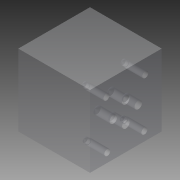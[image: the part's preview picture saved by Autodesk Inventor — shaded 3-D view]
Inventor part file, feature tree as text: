
AUTODESK INVENTOR PART (.ipt)
format: ipt  version: 2014 (Build 180170000, 170)  size: 209,920 bytes
history: native  units: mm
features: other x48, extrude x15, sketch x15
ambient origin geometry x8: Origin, YZ Plane, XZ Plane, XY Plane, X Axis, Y Axis, Z Axis, Center Point
bodies: 实体1 (feature_tree)
feature tree (78):
  extrude  "拉伸1"  Depth=51.0mm
  other  "UCS1"
  other  "UCS2"
  other  "UCS3"
  other  "UCS4"
  other  "UCS5"
  other  "UCS6"
  extrude  "拉伸2"  Depth=30.0mm
  extrude  "拉伸3"  Depth=4.25mm
  extrude  "拉伸4"  Depth=21.5mm
  extrude  "拉伸5"  Depth=0.75mm
  extrude  "拉伸6"  TaperAngle=0.0deg  [1 undecoded]
  extrude  "拉伸7"  Depth=31.75mm
  extrude  "拉伸8"  Depth=18.5mm
  extrude  "拉伸9"  Depth=16.0mm
  extrude  "拉伸10"  Depth=16.0mm
  extrude  "拉伸11"  Depth=16.0mm
  extrude  "拉伸12"  Depth=16.0mm TaperAngle=0.0deg
  extrude  "拉伸13"  Depth=16.0mm
  extrude  "拉伸14"  Depth=16.0mm
  extrude  "拉伸15"  Depth=16.0mm
  sketch  "草图1"  dims[d0=60.0mm d1=0.0mm]
  sketch  "草图2"  dims[d2=0.0mm d3=0.0mm d4=0.0mm d5=0.0mm d6=0.0mm d7=0.0mm]
  sketch  "草图3"  dims[d8=0.0mm d9=0.0mm d10=0.0mm d11=0.0mm d12=0.0mm d13=0.0mm]
  sketch  "草图4"  dims[d14=0.0mm d15=0.0mm d16=0.0mm d17=0.0mm d18=0.0mm d19=0.0mm]
  sketch  "草图5"  dims[d20=0.0mm d21=0.0mm d22=0.0mm d23=0.0mm d24=0.0mm d25=0.0mm]
  sketch  "草图6"  dims[d26=0.0mm d27=0.0mm d28=0.0mm d29=0.0mm d30=0.0mm d31=0.0mm]
  sketch  "草图7"  dims[d32=0.0mm d33=0.0mm d34=0.0mm d35=0.0mm d36=0.0mm d37=0.0mm d38=51.0mm]
  sketch  "草图8"  dims[d39=43.0mm d40=30.0mm]
  sketch  "草图9"  dims[d41=29.0mm d42=4.25mm]
  sketch  "草图10"  dims[d43=15.5mm d44=21.5mm]
  sketch  "草图11"  dims[d45=40.5mm d46=0.75mm]
  sketch  "草图12"  dims[d47=40.5mm d49=0.0mm]
  sketch  "草图13"  dims[d50=31.0mm d51=31.75mm]
  sketch  "草图14"  dims[d52=18.5mm d53=0.0mm d54=18.5mm d55=-10.297443mm]
  sketch  "草图15"  dims[d56=18.5mm d57=-10.297443mm d58=18.5mm d59=-10.297443mm d60=18.5mm d61=-10.297443mm d62=5.0mm d63=16.0mm d64=0.0mm d65=6.3mm d66=25.9mm d67=21.5mm d68=10.7mm d69=0.0mm d70=10.7mm d71=-10.297443mm d72=6.3mm d73=21.5mm d74=5.1mm d75=13.7mm d76=0.0mm d77=13.7mm d78=-10.297443mm d79=6.3mm d80=12.7mm d81=15.5mm d82=11.7mm d83=0.0mm d84=11.7mm d85=-10.297443mm d86=6.3mm d87=15.5mm d88=30.2mm d89=12.7mm d90=0.0mm d91=12.7mm d92=-10.297443mm]
  other  "UCS1: YZ 平面"
  other  "UCS1: XZ 平面"
  other  "UCS1: XY 平面"
  other  "UCS1: X 轴"
  other  "UCS1: Y 轴"
  other  "UCS1: Z 轴"
  other  "UCS1: 原点"
  other  "UCS2: YZ 平面"
  other  "UCS2: XZ 平面"
  other  "UCS2: XY 平面"
  other  "UCS2: X 轴"
  other  "UCS2: Y 轴"
  other  "UCS2: Z 轴"
  other  "UCS2: 原点"
  other  "UCS3: YZ 平面"
  other  "UCS3: XZ 平面"
  other  "UCS3: XY 平面"
  other  "UCS3: X 轴"
  other  "UCS3: Y 轴"
  other  "UCS3: Z 轴"
  other  "UCS3: 原点"
  other  "UCS4: YZ 平面"
  other  "UCS4: XZ 平面"
  other  "UCS4: XY 平面"
  other  "UCS4: X 轴"
  other  "UCS4: Y 轴"
  other  "UCS4: Z 轴"
  other  "UCS4: 原点"
  other  "UCS5: YZ 平面"
  other  "UCS5: XZ 平面"
  other  "UCS5: XY 平面"
  other  "UCS5: X 轴"
  other  "UCS5: Y 轴"
  other  "UCS5: Z 轴"
  other  "UCS5: 原点"
  other  "UCS6: YZ 平面"
  other  "UCS6: XZ 平面"
  other  "UCS6: XY 平面"
  other  "UCS6: X 轴"
  other  "UCS6: Y 轴"
  other  "UCS6: Z 轴"
  other  "UCS6: 原点"
note: 1 required parameter value undecoded (feature->parameter linkage not recoverable at this tier; creation-order binding heuristic only, values carry confidence <= 0.55)
